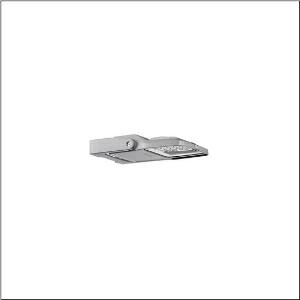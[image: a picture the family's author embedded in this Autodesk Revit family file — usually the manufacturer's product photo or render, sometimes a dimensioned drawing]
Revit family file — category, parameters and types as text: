
# Revit family: floodlight_fl_21_iq_micro___pl33t_5xa7762a4f2a_0497
name_source: partatom
category: Lighting Fixtures
units: mm (PartAtom-declared; Revit-internal decimal feet)

## family parameters
Cut with Voids When Loaded = No
Host = Face
Light Source = No
Part Type = Normal
Room Calculation Point = No
Round Connector Dimension = Use Diameter
Shared = No

## types (1)
- --- (1 x LED, 3050 lm, 23.1 W, 4000K)
    Apparent Load = 23 VA
    CIE Flux Codes = 26 75 99 100 100
    Color Rendering = 70
    Color Temperature = 4000K
    Default Elevation = 1800 mm
    Description = Floodlight FL 21 iQ micro, floodlight, primary light control with lens, of PMMA, primary optical cover: protective disc, of toughened safety glass, transparent, light distribution: PL33T, light emission: direct distribution, installation type: surface-mounted, LED, High Power LED, rated luminous flux: 3.050lm, luminous efficacy: 132lm/W, light colour: 740, colour temperature: 4000K, control: Auto-Match, Temp-Guard, Night-Set, Smart-Wire, Desk-Remote (wireless, voltage-free reading and setting of iQ features in the workshop via application-optimized NFC function/RFID function), optimised constant luminous flux control (CLO 2.0), Street-Remote, with terminal, 6-pole, mains connection: 220..240V, AC, 50/60Hz, start of lifetime: 23W, end of service life: 24W, reduction: 11W, luminaire housing, of diecast aluminium, powder-coated, Siteco® metallic grey (DB 702S), corrosivity category C5 mid according to DIN EN ISO 12944, sealing non-destructively replaceable, design bracket, of diecast aluminium, powder-coated, Siteco® metallic grey (DB 702S), protection rating (complete): IP66, insulation class (complete): insulation class II (safety insulation), certification: CE, ENEC, VDE, protection symbol: D, impact resistance: IK07, permissible operating ambient temperature: -40..+40°C, permissible operating ambient temperature for outdoor applications: -40..+50°C, standard: DIN EN 12944, LABS conformity tested according to VDMA 24364:2018-05, packaging unit: 1 piece

Light Distribution: PL33T
    Height = 65 mm
    Lamp = 1 x LED
    Lamp Light Flux = 3050 lm
    Lamp Power = 23.1 W
    Lamp count = 1
    Length = 312 mm
    Luminous efficacy = 132 lm/W
    Manufacturer = Siteco
    ModVariant = No
    Model = 5XA7762A4F2A
    Mounting Place = Wall
    Mounting Type = Surface mounted
    Number of Poles = 1
    OnlyDefault = Yes
    Power Factor = 1
    Product Name = Floodlight FL 21 iQ micro | PL33T
    Product group = floodlight | wall mounted
    ProductGroupID = 2001
    Protection Class = Protection class II
    Protection Degree = IP 66
    RLX_Detail_Level = 1
    RLX_Emergency_Light_Flux = 0 lm
    RLX_Emergency_Type = 0
    RLX_Emergency_Type_DB = No
    RlxData = <blob elided: 97641 chars, md5=de532ab8>
    Socket = socket
    Standby Power = 0 W
    System Light Flux = 3050 lm
    System Power = 23 W
    Type Comments = factory setting: luminous flux: 100 % | dim-lin: 254 | 455 mA
    Type Image = l_1006878.jpg
    URL = http://relux.com
    VarID = @adj_080385
    Voltage = 0 V
    Weight = 0.00 kg
    Width = 230 mm

## geometry (parser evidence)
native form markers: Blend x4, Sweep x11
no freeform markers — native parametric forms only
